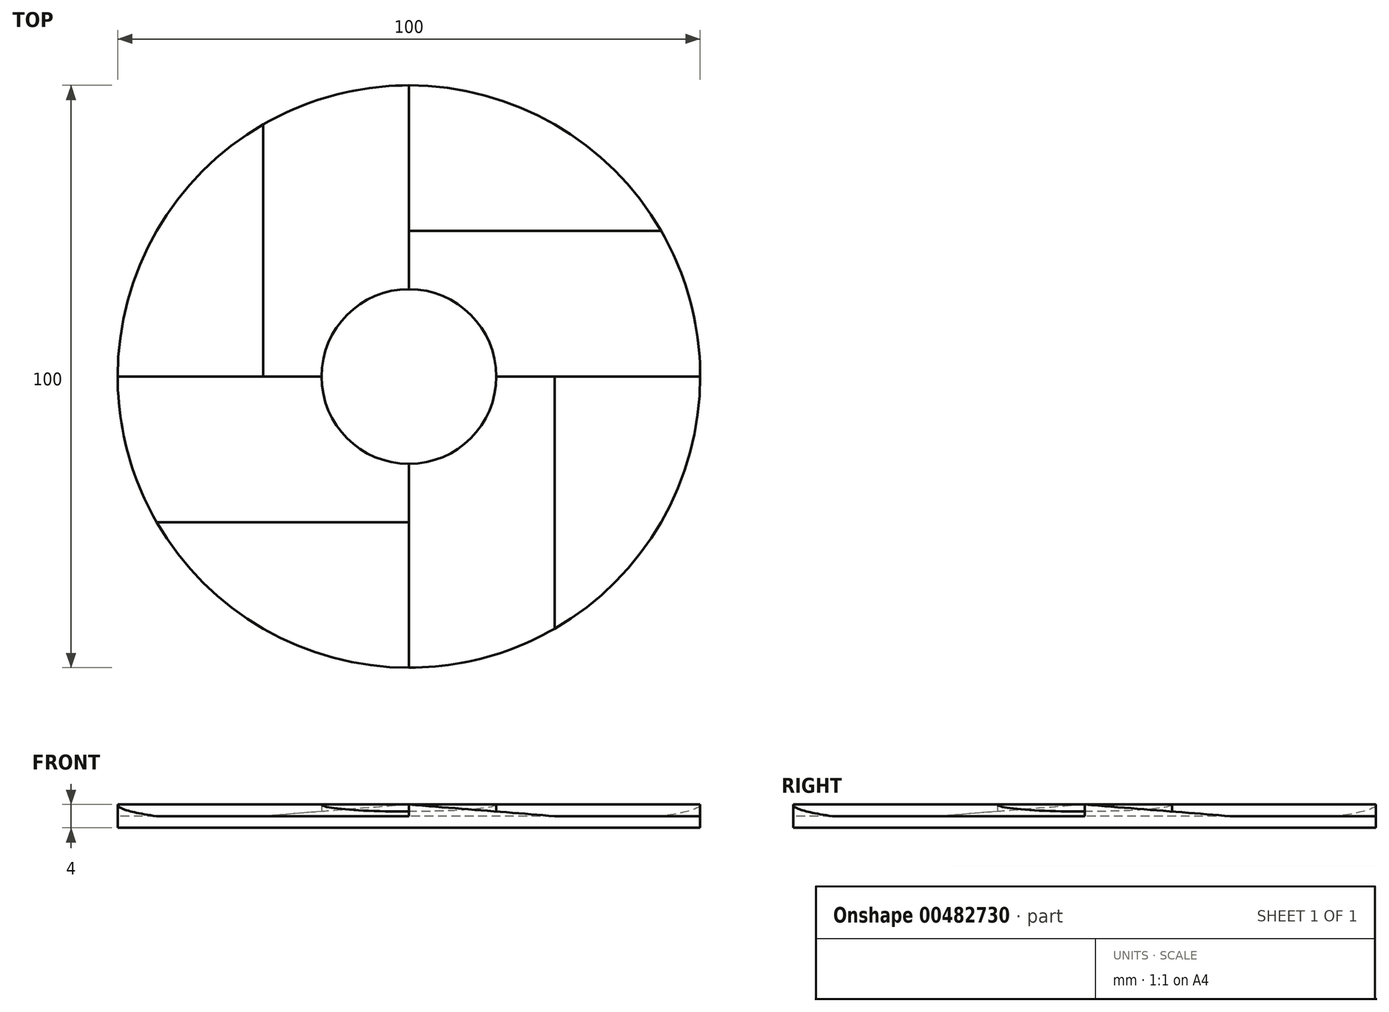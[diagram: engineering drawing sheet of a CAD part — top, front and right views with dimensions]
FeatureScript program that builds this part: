
annotation { "Feature Type Name" : "Feature", "Feature Type Description" : "" }
export const myFeature = defineFeature(function(context is Context, id is Id, definition is map)
    precondition{}
    {
        {
            var Q0;
            Q0=qCreatedBy(makeId("Top.planeOp"),FACE);
            var sketch = newSketch(context, id + "F0", { "sketchPlane" : qUnion([Q0])});
            skCircle(sketch, "E0", {"center": v(0, 0) * mm, "radius": 50 * mm});
            skCircle(sketch, "E1", {"center": v(0, 0) * mm, "radius": 15 * mm});
            skSolve(sketch);
        }
        {
            var Q0;
            Q0=makeQuery(id+"F0.imprint","IMPRINT",FACE,{"disambiguationData":[TD([[makeQuery(id+"F0.imprint","IMPRINT",EDGE,{"derivedFrom":sQuery(id+"F0.wireOp",EDGE,"E0")}),1.0]])]});
            extrude(context, id + "F1", {"entities" : qUnion([Q0]), "depth" : 3 * mm, "offsetDistance" : 25 * mm});
        }
        {
            var Q0;
            Q0=makeQuery(id+"F0.imprint","IMPRINT",FACE,{"disambiguationData":[TD([[makeQuery(id+"F0.imprint","IMPRINT",EDGE,{"derivedFrom":sQuery(id+"F0.wireOp",EDGE,"E1")}),1.0]])]});
            extrude(context, id + "F2", {"entities" : qUnion([Q0]), "operationType" : NewBodyOperationType.ADD, "depth" : 5 * mm, "offsetDistance" : 25 * mm});
        }
        {
            var Q0;
            Q0=qCreatedBy(makeId("Front.planeOp"),FACE);
            var sketch = newSketch(context, id + "F3", { "sketchPlane" : qUnion([Q0])});
            skLineSegment(sketch, "E2.0", {"start": v(-50, 3) * mm, "end": v(50, 3) * mm, "construction": true});
            skLineSegment(sketch, "E3", {"start": v(0, 3) * mm, "end": v(0, 5) * mm});
            skLineSegment(sketch, "E4", {"start": v(0, 5) * mm, "end": v(25, 3) * mm});
            skLineSegment(sketch, "E5", {"start": v(25, 3) * mm, "end": v(0, 3) * mm});
            skSolve(sketch);
        }
        {
            var Q0;
            Q0=makeQuery(id+"F3.imprint","IMPRINT",FACE,{"disambiguationData":[TD([[makeQuery(id+"F3.imprint","IMPRINT",EDGE,{"derivedFrom":sQuery(id+"F3.wireOp",EDGE,"E3")}),-1.0]])]});
            extrude(context, id + "F4", {"entities" : qUnion([Q0]), "operationType" : NewBodyOperationType.ADD, "depth" : 50 * mm, "offsetDistance" : 25 * mm});
        }
        {
            var Q0;
            Q0=makeQuery(id+"F1.opExtrude","SWEPT_BODY",BODY,{"disambiguationData":[OSD([sQuery(id+"F0.wireOp",EDGE,"E0"),sQuery(id+"F0.wireOp",EDGE,"E1")])]});
            var Q1;
            {var subQ0=sQuery(id+"F0.wireOp",EDGE,"E0");Q1=makeQuery(id+"F4.boolean.opBoolean","SPLIT",EDGE,{"disambiguationData":[topologyDisambiguationEdgeConnected([makeQuery(id+"F1.opExtrude","CAP_FACE",FACE,{"disambiguationData":[OSD([subQ0,sQuery(id+"F0.wireOp",EDGE,"E1")])],"isStart":false})])],"derivedFrom":makeQuery(id+"F1.opExtrude","CAP_EDGE",EDGE,{"disambiguationData":[OSD([subQ0])],"isStart":false})});}
            circularPattern(context, id + "F5", {"operationType" : NewBodyOperationType.ADD, "entities" : qUnion([Q0]), "axis" : qUnion([Q1]), "angle" : 360 * degree, "instanceCount" : 4, "equalSpace" : true});
        }
        {
            var Q0;
            Q0=qCreatedBy(makeId("Top.planeOp"),FACE);
            var sketch = newSketch(context, id + "F6", { "sketchPlane" : qUnion([Q0])});
            skCircle(sketch, "E6", {"center": v(0, 0) * mm, "radius": 62.5 * mm});
            skCircle(sketch, "E7", {"center": v(0, 0) * mm, "radius": 50 * mm});
            skSolve(sketch);
        }
        {
            var Q0;
            Q0=makeQuery(id+"F6.imprint","IMPRINT",FACE,{"disambiguationData":[TD([[makeQuery(id+"F6.imprint","IMPRINT",EDGE,{"derivedFrom":sQuery(id+"F6.wireOp",EDGE,"E6")}),1.0]])]});
            extrude(context, id + "F7", {"entities" : qUnion([Q0]), "operationType" : NewBodyOperationType.REMOVE, "depth" : 25 * mm, "offsetDistance" : 25 * mm});
        }
        {
            var Q0;
            Q0=qCreatedBy(makeId("Front.planeOp"),FACE);
            var sketch = newSketch(context, id + "F8", { "sketchPlane" : qUnion([Q0])});
            skLineSegment(sketch, "E8.bottom", {"start": v(100, -1) * mm, "end": v(-100, -1) * mm});
            skLineSegment(sketch, "E8.top", {"start": v(100, 1) * mm, "end": v(-100, 1) * mm});
            skLineSegment(sketch, "E8.left", {"start": v(100, -1) * mm, "end": v(100, 1) * mm});
            skLineSegment(sketch, "E8.right", {"start": v(-100, -1) * mm, "end": v(-100, 1) * mm});
            skPoint(sketch, "E8.middle", {"position": v(0, 0) * mm});
            skSolve(sketch);
        }
        {
            var Q0;
            Q0=makeQuery(id+"F8.imprint","IMPRINT",FACE,{"disambiguationData":[TD([[makeQuery(id+"F8.imprint","IMPRINT",EDGE,{"derivedFrom":sQuery(id+"F8.wireOp",EDGE,"E8.bottom")}),-1.0]])]});
            extrude(context, id + "F9", {"entities" : qUnion([Q0]), "operationType" : NewBodyOperationType.REMOVE, "oppositeDirection" : true, "depth" : 100 * mm, "offsetDistance" : 25 * mm, "hasSecondDirection" : true, "secondDirectionOppositeDirection" : false, "secondDirectionDepth" : 100 * mm});
        }
    });
